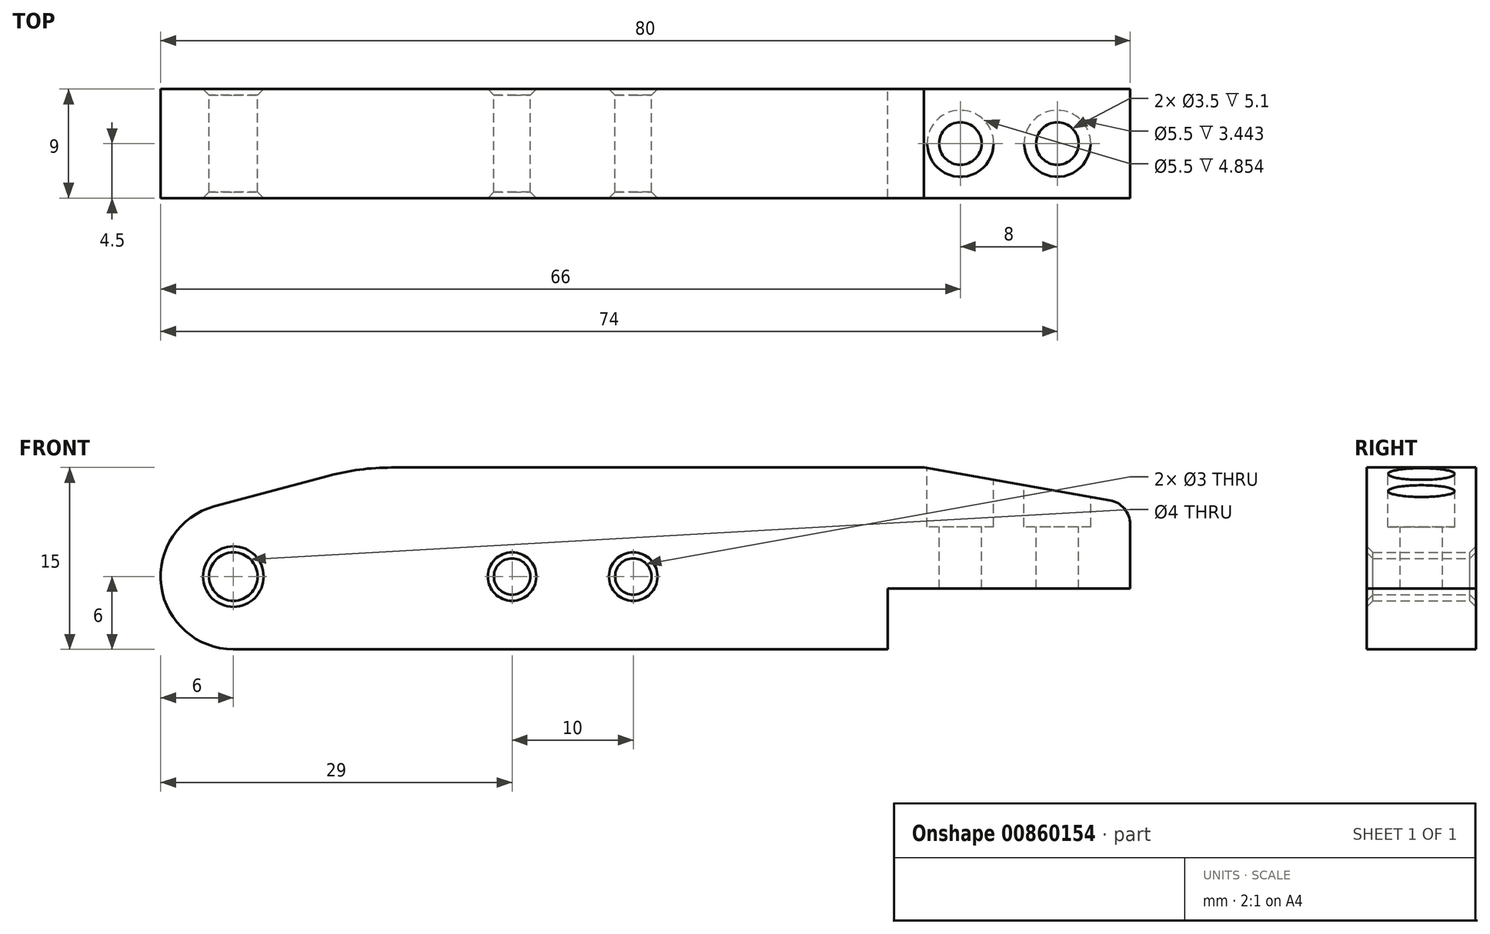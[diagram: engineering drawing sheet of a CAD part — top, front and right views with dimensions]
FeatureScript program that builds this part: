
annotation { "Feature Type Name" : "Feature", "Feature Type Description" : "" }
export const myFeature = defineFeature(function(context is Context, id is Id, definition is map)
    precondition{}
    {
        {
            var Q0;
            Q0=qCreatedBy(makeId("Front.planeOp"),FACE);
            var sketch = newSketch(context, id + "F0", { "sketchPlane" : qUnion([Q0])});
            skArc(sketch, "E0", {"start": v(-1.55, 5.8) * mm, "mid": v(-5.95, -0.78) * mm, "end": v(0, -6) * mm});
            skLineSegment(sketch, "E1", {"start": v(-1.55, 5.8) * mm, "end": v(10.4, 9) * mm});
            skLineSegment(sketch, "E2", {"start": v(10.4, 9) * mm, "end": v(56.99, 9) * mm});
            skLineSegment(sketch, "E3", {"start": v(56.99, 9) * mm, "end": v(74, 6) * mm});
            skLineSegment(sketch, "E4", {"start": v(74, 6) * mm, "end": v(74, -1) * mm});
            skLineSegment(sketch, "E5", {"start": v(74, -1) * mm, "end": v(54, -1) * mm});
            skLineSegment(sketch, "E6", {"start": v(54, -1) * mm, "end": v(54, -6) * mm});
            skLineSegment(sketch, "E7", {"start": v(54, -6) * mm, "end": v(0, -6) * mm});
            skCircle(sketch, "E8", {"center": v(0, 0) * mm, "radius": 2 * mm});
            skCircle(sketch, "E9", {"center": v(23, 0) * mm, "radius": 1.5 * mm});
            skCircle(sketch, "E10", {"center": v(33, 0) * mm, "radius": 1.5 * mm});
            skSolve(sketch);
        }
        {
            var Q0;
            Q0=makeQuery(id+"F0.imprint","IMPRINT",FACE,{"disambiguationData":[TD([[makeQuery(id+"F0.imprint","IMPRINT",EDGE,{"derivedFrom":sQuery(id+"F0.wireOp",EDGE,"E0")}),1.0]])]});
            extrude(context, id + "F1", {"entities" : qUnion([Q0]), "endBound" : BoundingType.SYMMETRIC, "depth" : 9 * mm, "offsetDistance" : 25 * mm});
        }
        {
            var Q0;
            Q0=makeQuery(id+"F1.opExtrude","SWEPT_EDGE",EDGE,{"disambiguationData":[OSD([sQuery(id+"F0.wireOp",EDGE,"E3"),sQuery(id+"F0.wireOp",EDGE,"E4")])]});
            fillet(context, id + "F2", {"entities" : qUnion([Q0]), "radius" : 2 * mm, "tangentPropagation" : true, "allowEdgeOverflow" : false});
        }
        {
            var Q0;
            Q0=makeQuery(id+"F1.opExtrude","SWEPT_EDGE",EDGE,{"disambiguationData":[OSD([sQuery(id+"F0.wireOp",EDGE,"E1"),sQuery(id+"F0.wireOp",EDGE,"E2")])]});
            fillet(context, id + "F3", {"entities" : qUnion([Q0]), "radius" : 20 * mm, "tangentPropagation" : true, "allowEdgeOverflow" : false});
        }
        {
            var Q0;
            Q0=makeQuery(id+"F1.opExtrude","CAP_EDGE",EDGE,{"disambiguationData":[OSD([sQuery(id+"F0.wireOp",EDGE,"E8")])],"isStart":false});
            var Q1;
            Q1=makeQuery(id+"F1.opExtrude","CAP_EDGE",EDGE,{"disambiguationData":[OSD([sQuery(id+"F0.wireOp",EDGE,"E9")])],"isStart":false});
            var Q2;
            Q2=makeQuery(id+"F1.opExtrude","CAP_EDGE",EDGE,{"disambiguationData":[OSD([sQuery(id+"F0.wireOp",EDGE,"E10")])],"isStart":false});
            var Q3;
            Q3=makeQuery(id+"F1.opExtrude","CAP_EDGE",EDGE,{"disambiguationData":[OSD([sQuery(id+"F0.wireOp",EDGE,"E8")])],"isStart":true});
            var Q4;
            Q4=makeQuery(id+"F1.opExtrude","CAP_EDGE",EDGE,{"disambiguationData":[OSD([sQuery(id+"F0.wireOp",EDGE,"E9")])],"isStart":true});
            var Q5;
            Q5=makeQuery(id+"F1.opExtrude","CAP_EDGE",EDGE,{"disambiguationData":[OSD([sQuery(id+"F0.wireOp",EDGE,"E10")])],"isStart":true});
            chamfer(context, id + "F4", {"entities" : qUnion([Q0, Q1, Q2, Q3, Q4, Q5]), "width" : 0.5 * mm, "tangentPropagation" : true});
        }
        {
            var Q0;
            Q0=makeQuery(id+"F1.opExtrude","SWEPT_FACE",FACE,{"disambiguationData":[OSD([sQuery(id+"F0.wireOp",EDGE,"E2")])]});
            var sketch = newSketch(context, id + "F5", { "sketchPlane" : qUnion([Q0])});
            skPoint(sketch, "E11", {"position": v(60, 0) * mm});
            skPoint(sketch, "E12", {"position": v(68, 0) * mm});
            skSolve(sketch);
        }
        {
            var Q0;
            Q0=sQuery(id+"F5.wireOp",VERTEX,"E11");
            var Q1;
            Q1=sQuery(id+"F5.wireOp",VERTEX,"E12");
            var Q2;
            Q2=makeQuery(id+"F1.opExtrude","SWEPT_BODY",BODY,{"disambiguationData":[OSD([sQuery(id+"F0.wireOp",EDGE,"E0"),sQuery(id+"F0.wireOp",EDGE,"E1"),sQuery(id+"F0.wireOp",EDGE,"E2"),sQuery(id+"F0.wireOp",EDGE,"E3"),sQuery(id+"F0.wireOp",EDGE,"E4"),sQuery(id+"F0.wireOp",EDGE,"E5"),sQuery(id+"F0.wireOp",EDGE,"E6"),sQuery(id+"F0.wireOp",EDGE,"E7"),sQuery(id+"F0.wireOp",EDGE,"E8"),sQuery(id+"F0.wireOp",EDGE,"E9"),sQuery(id+"F0.wireOp",EDGE,"E10")])]});
            hole(context, id + "F6", {"style" : HoleStyle.C_BORE, "endStyle" : HoleEndStyle.THROUGH, "holeDiameter" : 3.5 * mm, "cBoreDiameter" : 5.5 * mm, "cBoreDepth" : 4.9 * mm, "majorDiameter" : 3 * mm, "isTappedThrough" : true, "tappedDepth" : 5.5 * mm, "tapClearance" : 3, "startFromSketch" : true, "locations" : qUnion([Q0, Q1]), "scope" : qUnion([Q2])});
        }
    });
